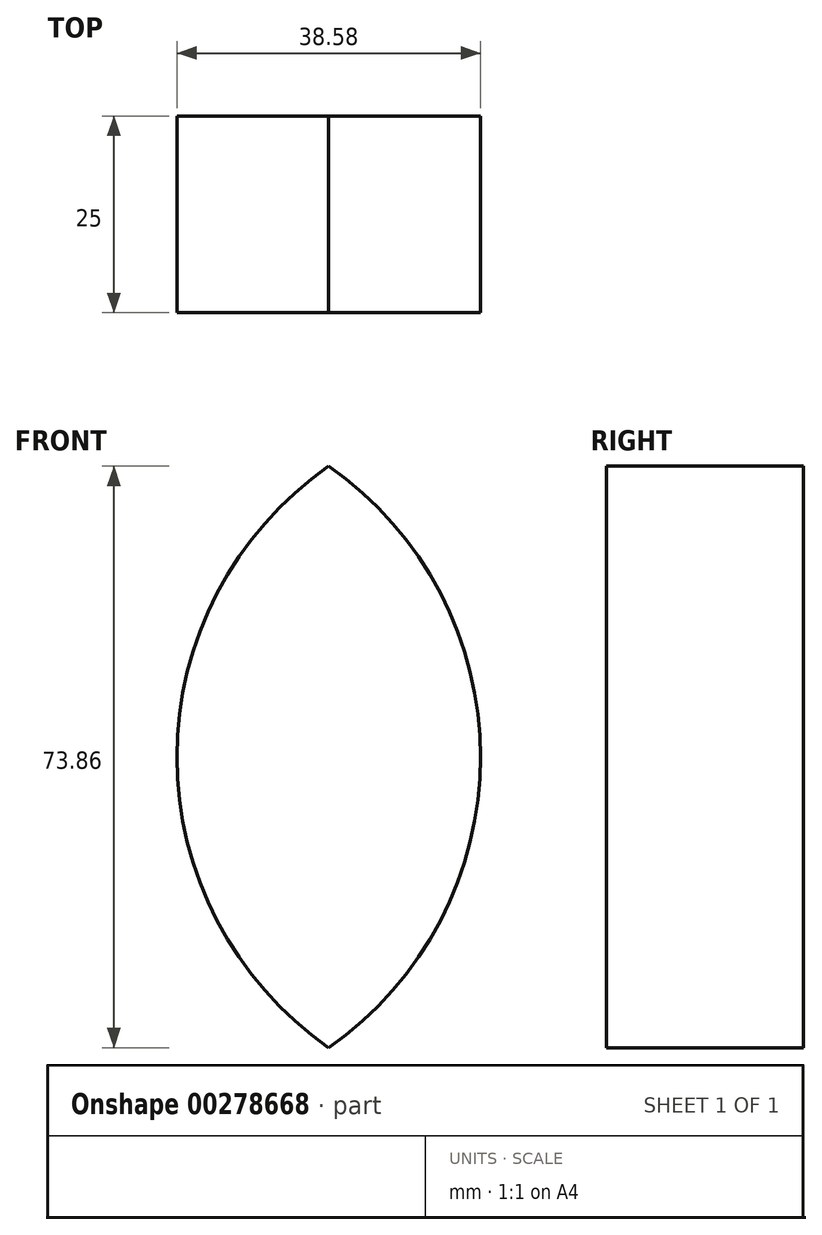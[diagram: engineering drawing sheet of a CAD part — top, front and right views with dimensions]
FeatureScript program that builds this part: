
annotation { "Feature Type Name" : "Feature", "Feature Type Description" : "" }
export const myFeature = defineFeature(function(context is Context, id is Id, definition is map)
    precondition{}
    {
        {
            var Q0;
            Q0=qCreatedBy(makeId("Front.planeOp"),FACE);
            var sketch = newSketch(context, id + "F0", { "sketchPlane" : qUnion([Q0])});
            skArc(sketch, "E0", {"start": v(0, -35.26) * mm, "mid": v(19.29, 1.67) * mm, "end": v(0, 38.6) * mm});
            skArc(sketch, "E1", {"start": v(0, 38.6) * mm, "mid": v(-19.29, 1.67) * mm, "end": v(0, -35.26) * mm});
            skSolve(sketch);
        }
        {
            var Q0;
            Q0 = qSketchRegion(id + "F0", true);
            extrude(context, id + "F1", {"entities" : qUnion([Q0]), "depth" : 25 * mm, "offsetDistance" : 25 * mm});
        }
    });
